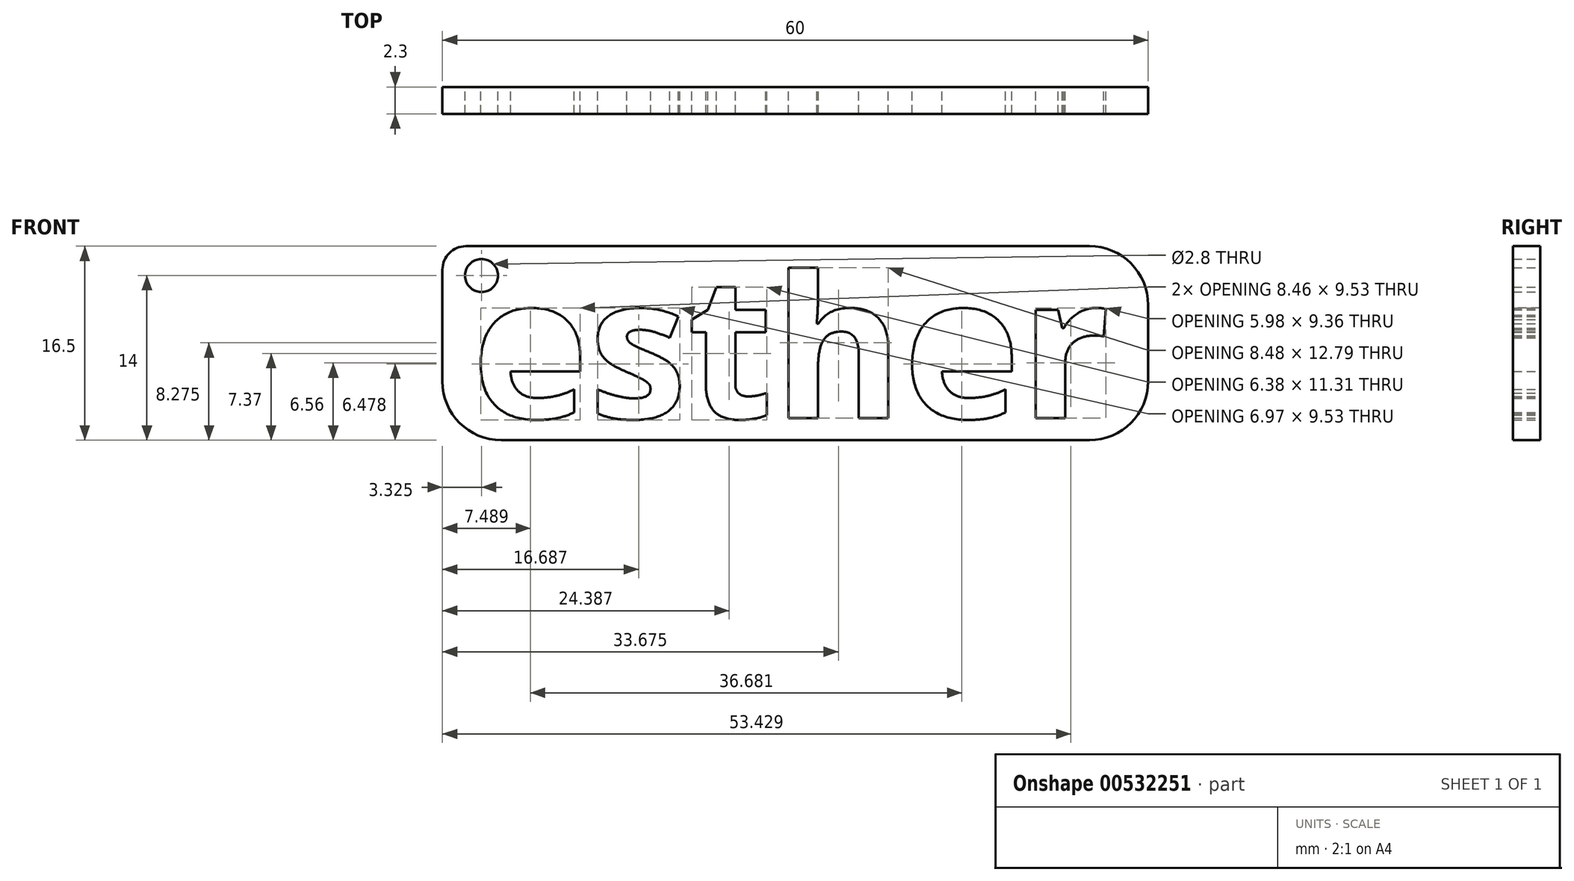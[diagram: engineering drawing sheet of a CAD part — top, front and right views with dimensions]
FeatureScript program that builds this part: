
annotation { "Feature Type Name" : "Feature", "Feature Type Description" : "" }
export const myFeature = defineFeature(function(context is Context, id is Id, definition is map)
    precondition{}
    {
        {
            var Q0;
            Q0=qCreatedBy(makeId("Front.planeOp"),FACE);
            var sketch = newSketch(context, id + "F0", { "sketchPlane" : qUnion([Q0])});
            skLineSegment(sketch, "E0.bottom", {"start": v(-28, 10) * mm, "end": v(25, 10) * mm});
            skLineSegment(sketch, "E0.top", {"start": v(-25, -6.5) * mm, "end": v(25, -6.5) * mm});
            skLineSegment(sketch, "E0.left", {"start": v(-30, 8) * mm, "end": v(-30, -1.5) * mm});
            skLineSegment(sketch, "E0.right", {"start": v(30, 5) * mm, "end": v(30, -1.5) * mm});
            skText(sketch, "E1", { "text": "esther", "fontName": "OpenSans-Bold.ttf"});
            skCircle(sketch, "E2", {"center": v(-26.68, 7.5) * mm, "radius": 1.4 * mm});
            skPoint(sketch, "E3.visualSharp", {"position": v(30, 10) * mm});
            skArc(sketch, "E3.filletArc", {"start": v(30, 5) * mm, "mid": v(28.54, 8.54) * mm, "end": v(25, 10) * mm});
            skPoint(sketch, "E4.visualSharp", {"position": v(30, -6.5) * mm});
            skArc(sketch, "E4.filletArc", {"start": v(25, -6.5) * mm, "mid": v(28.54, -5.04) * mm, "end": v(30, -1.5) * mm});
            skPoint(sketch, "E5.visualSharp", {"position": v(-30, -6.5) * mm});
            skArc(sketch, "E5.filletArc", {"start": v(-30, -1.5) * mm, "mid": v(-28.54, -5.04) * mm, "end": v(-25, -6.5) * mm});
            skPoint(sketch, "E6.visualSharp", {"position": v(-30, 10) * mm});
            skArc(sketch, "E6.filletArc", {"start": v(-28, 10) * mm, "mid": v(-29.41, 9.41) * mm, "end": v(-30, 8) * mm});
            const initialGuessF0  = {"E1": [-0.0275, -0.00462, 1, 0, 0.01212]};
            skSetInitialGuess(sketch, initialGuessF0);
            skSolve(sketch);
        }
        {
            var Q0;
            Q0 = qSketchRegion(id + "F0", true);
            extrude(context, id + "F1", {"entities" : qUnion([Q0]), "depth" : 2.3 * mm, "offsetDistance" : 25 * mm});
        }
    });
